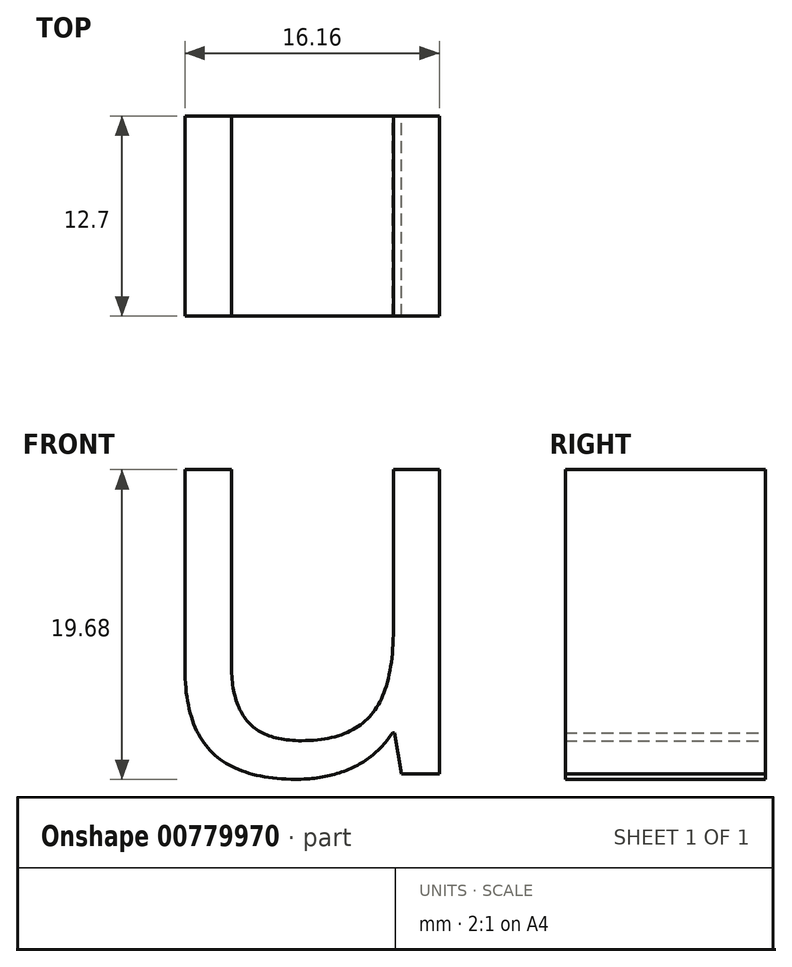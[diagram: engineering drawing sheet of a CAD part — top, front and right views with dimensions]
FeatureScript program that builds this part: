
annotation { "Feature Type Name" : "Feature", "Feature Type Description" : "" }
export const myFeature = defineFeature(function(context is Context, id is Id, definition is map)
    precondition{}
    {
        {
            var Q0;
            Q0=qCreatedBy(makeId("Front.planeOp"),FACE);
            var sketch = newSketch(context, id + "F0", { "sketchPlane" : qUnion([Q0])});
            skText(sketch, "E0", { "text": "u", "fontName": "OpenSans-Regular.ttf"});
            const initialGuessF0  = {"E0": [-0.05937, 0.0034, 1, 0, 0.02599]};
            skSetInitialGuess(sketch, initialGuessF0);
            skSolve(sketch);
        }
        {
            var Q0;
            Q0 = qSketchRegion(id + "F0", true);
            extrude(context, id + "F1", {"entities" : qUnion([Q0]), "depth" : 12.7 * mm, "offsetDistance" : 25.4 * mm});
        }
    });
